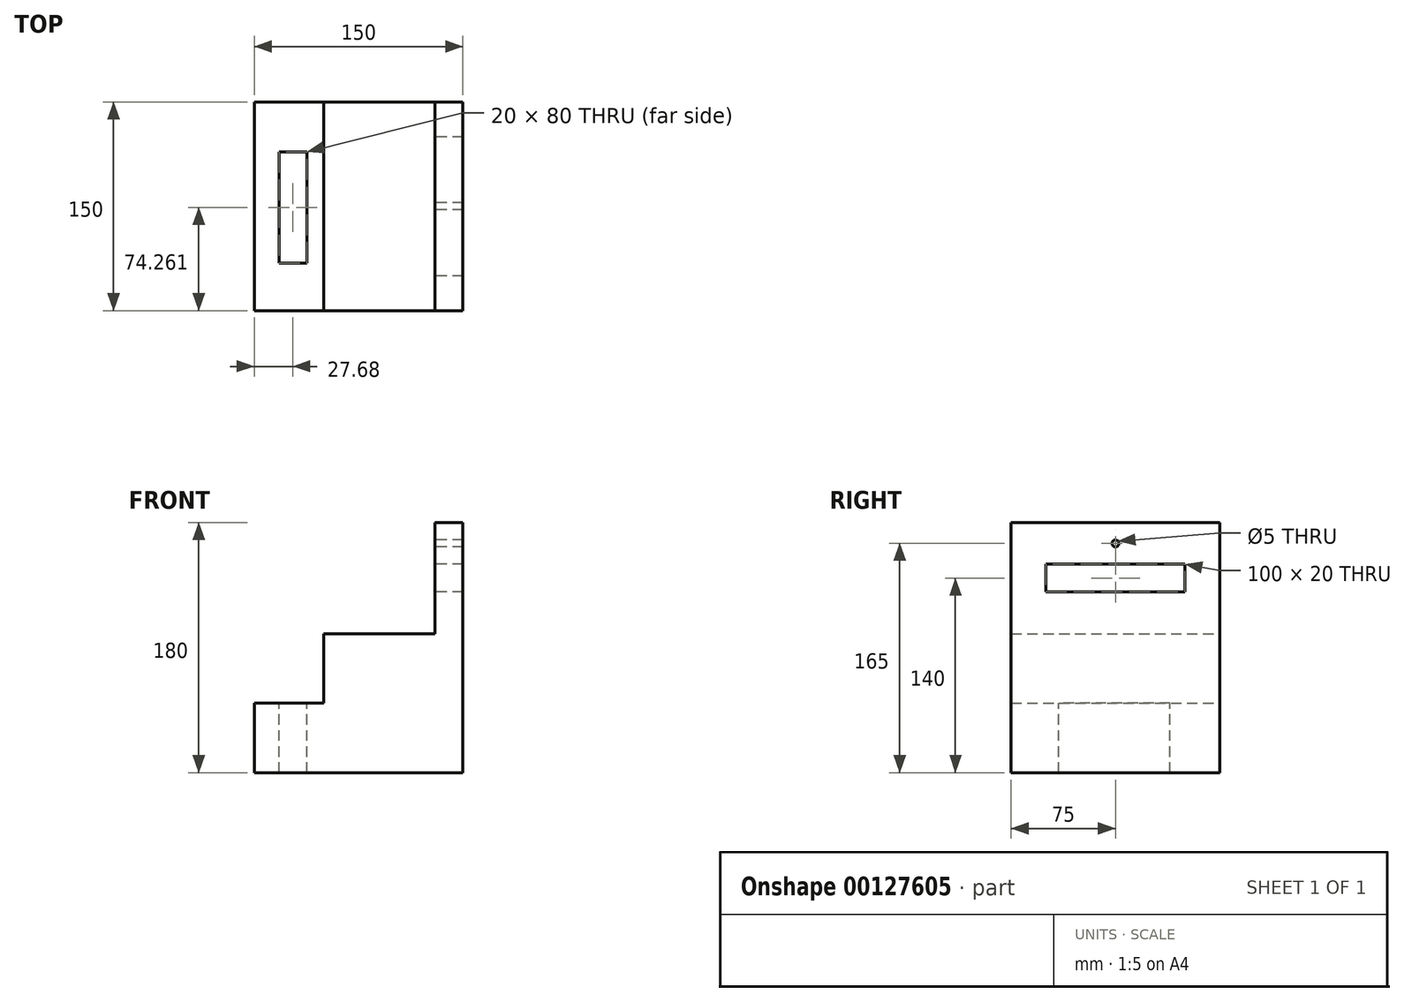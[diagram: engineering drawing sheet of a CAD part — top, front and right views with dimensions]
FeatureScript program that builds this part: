
annotation { "Feature Type Name" : "Feature", "Feature Type Description" : "" }
export const myFeature = defineFeature(function(context is Context, id is Id, definition is map)
    precondition{}
    {
        {
            var Q0;
            Q0=qCreatedBy(makeId("Front.planeOp"),FACE);
            var sketch = newSketch(context, id + "F0", { "sketchPlane" : qUnion([Q0])});
            skLineSegment(sketch, "E0.bottom", {"start": v(75, 90) * mm, "end": v(55, 90) * mm});
            skLineSegment(sketch, "E0.top", {"start": v(75, -90) * mm, "end": v(-75, -90) * mm});
            skLineSegment(sketch, "E0.left", {"start": v(75, 90) * mm, "end": v(75, -90) * mm});
            skLineSegment(sketch, "E0.right", {"start": v(-75, -40) * mm, "end": v(-75, -90) * mm});
            skPoint(sketch, "E0.middle", {"position": v(0, 0) * mm});
            skLineSegment(sketch, "E1", {"start": v(55, 90) * mm, "end": v(55, 0) * mm});
            skLineSegment(sketch, "E2", {"start": v(-25, 10) * mm, "end": v(-25, -40) * mm});
            skLineSegment(sketch, "E3", {"start": v(-25, -40) * mm, "end": v(-75, -40) * mm});
            skPoint(sketch, "E4.orphan", {"position": v(-75, 90) * mm});
            skLineSegment(sketch, "E5", {"start": v(-25, 10) * mm, "end": v(55, 10) * mm});
            skSolve(sketch);
        }
        {
            var Q0;
            Q0 = qSketchRegion(id + "F0", true);
            extrude(context, id + "F1", {"entities" : qUnion([Q0]), "depth" : 150 * mm});
        }
        {
            var Q0;
            Q0=makeQuery(id+"F1.opExtrude","SWEPT_FACE",FACE,{"disambiguationData":[OSD([sQuery(id+"F0.wireOp",EDGE,"E1")])]});
            var sketch = newSketch(context, id + "F2", { "sketchPlane" : qUnion([Q0])});
            skPoint(sketch, "E6.middle", {"position": v(100.02, 49.31) * mm});
            skLineSegment(sketch, "E7.bottom", {"start": v(25, 60) * mm, "end": v(125, 60) * mm});
            skLineSegment(sketch, "E7.top", {"start": v(25, 40) * mm, "end": v(125, 40) * mm});
            skLineSegment(sketch, "E7.left", {"start": v(25, 60) * mm, "end": v(25, 40) * mm});
            skLineSegment(sketch, "E7.right", {"start": v(125, 60) * mm, "end": v(125, 40) * mm});
            skSolve(sketch);
        }
        {
            var Q0;
            Q0 = qSketchRegion(id + "F2", true);
            extrude(context, id + "F3", {"entities" : qUnion([Q0]), "operationType" : NewBodyOperationType.REMOVE, "endBound" : BoundingType.THROUGH_ALL, "oppositeDirection" : true, "depth" : 25.4 * mm});
        }
        {
            var Q0;
            Q0=makeQuery(id+"F1.opExtrude","SWEPT_FACE",FACE,{"disambiguationData":[OSD([sQuery(id+"F0.wireOp",EDGE,"E1")])]});
            var sketch = newSketch(context, id + "F4", { "sketchPlane" : qUnion([Q0])});
            skCircle(sketch, "E8", {"center": v(75, 75) * mm, "radius": 2.5 * mm});
            skPoint(sketch, "E8.centerSnap0", {"position": v(75, 90) * mm});
            skSolve(sketch);
        }
        {
            var Q0;
            Q0=makeQuery(id+"F4.imprint","IMPRINT",FACE,{"disambiguationData":[TD([[makeQuery(id+"F4.imprint","IMPRINT",EDGE,{"derivedFrom":sQuery(id+"F4.wireOp",EDGE,"E8")}),1.0]])]});
            extrude(context, id + "F5", {"entities" : qUnion([Q0]), "operationType" : NewBodyOperationType.REMOVE, "endBound" : BoundingType.THROUGH_ALL, "oppositeDirection" : true, "depth" : 25.4 * mm});
        }
        {
            var Q0;
            Q0=makeQuery(id+"F1.opExtrude","SWEPT_FACE",FACE,{"disambiguationData":[OSD([sQuery(id+"F0.wireOp",EDGE,"E3")])]});
            var sketch = newSketch(context, id + "F6", { "sketchPlane" : qUnion([Q0])});
            skLineSegment(sketch, "E9.bottom", {"start": v(-37.32, -35.74) * mm, "end": v(-57.32, -35.74) * mm});
            skLineSegment(sketch, "E9.top", {"start": v(-37.32, -115.74) * mm, "end": v(-57.32, -115.74) * mm});
            skLineSegment(sketch, "E9.left", {"start": v(-37.32, -35.74) * mm, "end": v(-37.32, -115.74) * mm});
            skLineSegment(sketch, "E9.right", {"start": v(-57.32, -35.74) * mm, "end": v(-57.32, -115.74) * mm});
            skSolve(sketch);
        }
        {
            var Q0;
            Q0 = qSketchRegion(id + "F6", true);
            extrude(context, id + "F7", {"entities" : qUnion([Q0]), "operationType" : NewBodyOperationType.ADD, "depth" : 25.4 * mm});
        }
        {
            var Q0;
            Q0=makeQuery(id+"F7.opExtrude","CAP_FACE",FACE,{"disambiguationData":[OSD([sQuery(id+"F6.wireOp",EDGE,"E9.bottom"),sQuery(id+"F6.wireOp",EDGE,"E9.top"),sQuery(id+"F6.wireOp",EDGE,"E9.left"),sQuery(id+"F6.wireOp",EDGE,"E9.right")])],"isStart":false});
            var sketch = newSketch(context, id + "F8", { "sketchPlane" : qUnion([Q0])});
            skSolve(sketch);
        }
        {
            var Q0;
            Q0 = qSketchRegion(id + "F8", true);
            var Q1;
            Q1=makeQuery(id+"F8.imprint","IMPRINT",FACE,{"disambiguationData":[TD([[makeQuery(id+"F8.imprint","IMPRINT",EDGE,{"derivedFrom":makeQuery(id+"F7.opExtrude","CAP_EDGE",EDGE,{"disambiguationData":[OSD([sQuery(id+"F6.wireOp",EDGE,"E9.bottom")])],"isStart":false})}),1.0]])]});
            extrude(context, id + "F9", {"entities" : qUnion([Q0, Q1]), "operationType" : NewBodyOperationType.REMOVE, "endBound" : BoundingType.THROUGH_ALL, "oppositeDirection" : true, "depth" : 25.4 * mm});
        }
    });
